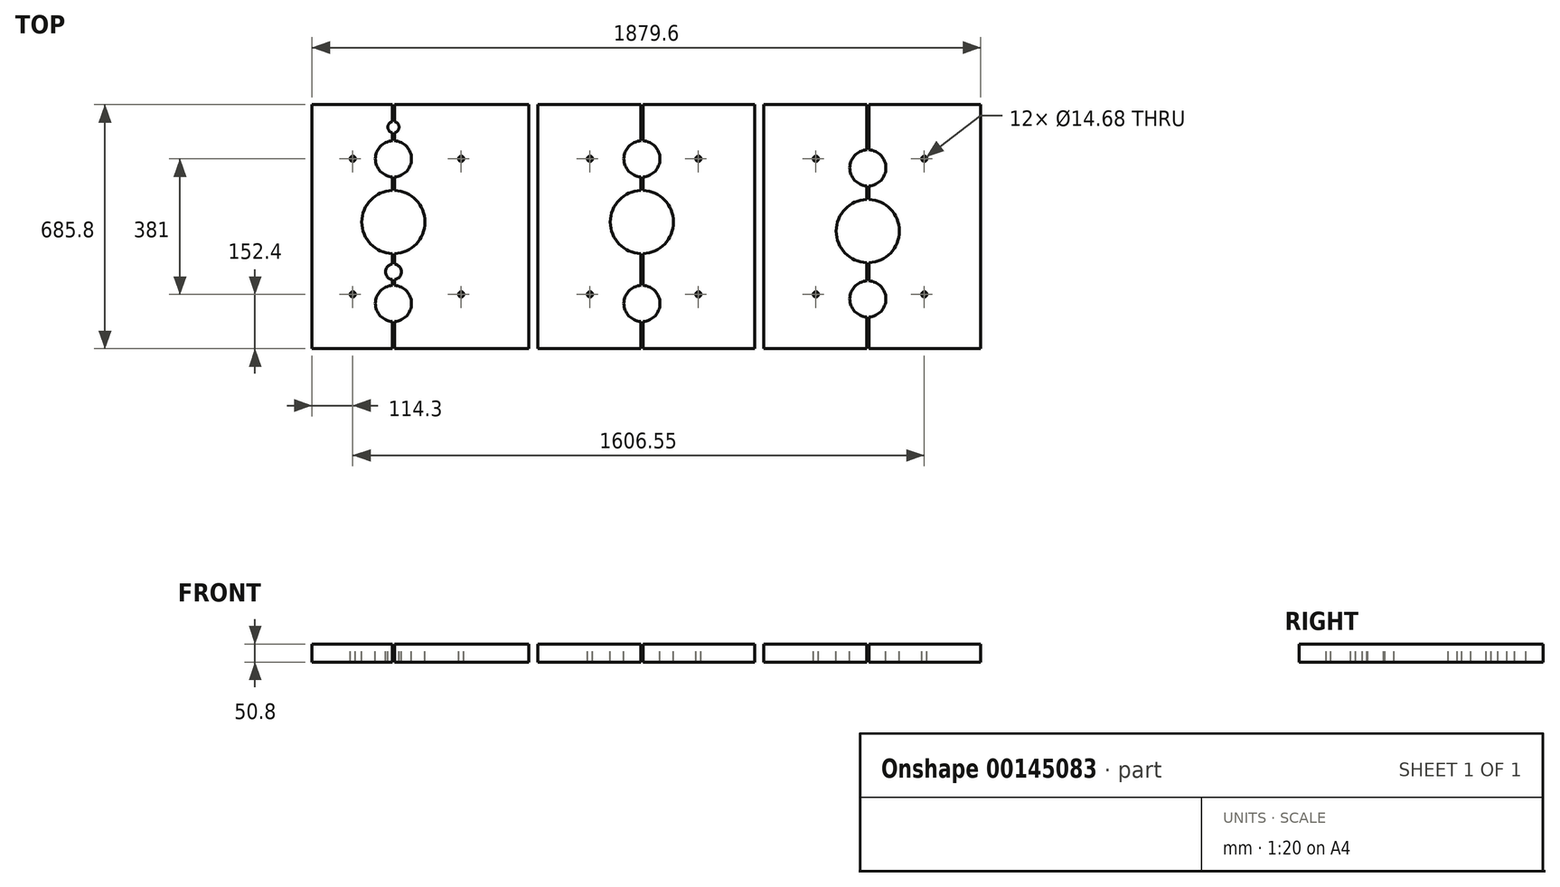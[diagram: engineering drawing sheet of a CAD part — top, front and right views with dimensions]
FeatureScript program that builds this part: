
annotation { "Feature Type Name" : "Feature", "Feature Type Description" : "" }
export const myFeature = defineFeature(function(context is Context, id is Id, definition is map)
    precondition{}
    {
        {
            var Q0;
            Q0=qCreatedBy(makeId("Top.planeOp"),FACE);
            var sketch = newSketch(context, id + "F0", { "sketchPlane" : qUnion([Q0])});
            skLineSegment(sketch, "E0.bottom", {"start": v(0, 685.8) * mm, "end": v(609.6, 685.8) * mm});
            skLineSegment(sketch, "E0.top", {"start": v(0, 0) * mm, "end": v(609.6, 0) * mm});
            skLineSegment(sketch, "E0.left", {"start": v(0, 685.8) * mm, "end": v(0, 0) * mm});
            skLineSegment(sketch, "E0.right", {"start": v(609.6, 685.8) * mm, "end": v(609.6, 0) * mm});
            skSolve(sketch);
        }
        {
            var Q0;
            Q0=makeQuery(id+"F0.imprint","IMPRINT",FACE,{"disambiguationData":[TD([[makeQuery(id+"F0.imprint","IMPRINT",EDGE,{"derivedFrom":sQuery(id+"F0.wireOp",EDGE,"E0.bottom")}),-1.0]])]});
            extrude(context, id + "F1", {"entities" : qUnion([Q0]), "oppositeDirection" : true, "depth" : 50.8 * mm});
        }
        {
            var Q0;
            Q0=makeQuery(id+"F1.opExtrude","CAP_FACE",FACE,{"disambiguationData":[OSD([sQuery(id+"F0.wireOp",EDGE,"E0.bottom"),sQuery(id+"F0.wireOp",EDGE,"E0.top"),sQuery(id+"F0.wireOp",EDGE,"E0.left"),sQuery(id+"F0.wireOp",EDGE,"E0.right")])],"isStart":true});
            var sketch = newSketch(context, id + "F2", { "sketchPlane" : qUnion([Q0])});
            skCircle(sketch, "E1", {"center": v(228.6, 533.4) * mm, "radius": 50.8 * mm});
            skCircle(sketch, "E2", {"center": v(228.6, 355.6) * mm, "radius": 88.9 * mm});
            skCircle(sketch, "E3", {"center": v(228.6, 622.3) * mm, "radius": 15.88 * mm});
            skCircle(sketch, "E4", {"center": v(228.6, 127) * mm, "radius": 50.8 * mm});
            skCircle(sketch, "E5", {"center": v(228.6, 215.9) * mm, "radius": 22.23 * mm});
            skLineSegment(sketch, "E6", {"start": v(114.3, 685.8) * mm, "end": v(114.3, 0) * mm, "construction": true});
            skLineSegment(sketch, "E7", {"start": v(419.1, 685.8) * mm, "end": v(419.1, 0) * mm, "construction": true});
            skPoint(sketch, "E8", {"position": v(419.1, 533.4) * mm});
            skPoint(sketch, "E9", {"position": v(114.3, 533.4) * mm});
            skPoint(sketch, "E10", {"position": v(419.1, 152.4) * mm});
            skPoint(sketch, "E11", {"position": v(114.3, 152.4) * mm});
            skPoint(sketch, "E12", {"position": v(228.6, 0) * mm});
            skLineSegment(sketch, "E13", {"start": v(228.6, 0) * mm, "end": v(0, 0) * mm, "construction": true});
            skLineSegment(sketch, "E14", {"start": v(228.6, 0) * mm, "end": v(609.6, 0) * mm, "construction": true});
            skSolve(sketch);
        }
        {
            var Q0;
            Q0=makeQuery(id+"F2.imprint","IMPRINT",FACE,{"disambiguationData":[TD([[makeQuery(id+"F2.imprint","IMPRINT",EDGE,{"derivedFrom":sQuery(id+"F2.wireOp",EDGE,"E1")}),1.0]])]});
            var Q1;
            Q1=makeQuery(id+"F2.imprint","IMPRINT",FACE,{"disambiguationData":[TD([[makeQuery(id+"F2.imprint","IMPRINT",EDGE,{"derivedFrom":sQuery(id+"F2.wireOp",EDGE,"E4")}),1.0]])]});
            var Q2;
            Q2=makeQuery(id+"F2.imprint","IMPRINT",FACE,{"disambiguationData":[TD([[makeQuery(id+"F2.imprint","IMPRINT",EDGE,{"derivedFrom":sQuery(id+"F2.wireOp",EDGE,"E2")}),1.0]])]});
            var Q3;
            Q3=makeQuery(id+"F2.imprint","IMPRINT",FACE,{"disambiguationData":[TD([[makeQuery(id+"F2.imprint","IMPRINT",EDGE,{"derivedFrom":sQuery(id+"F2.wireOp",EDGE,"E3")}),1.0]])]});
            var Q4;
            Q4=makeQuery(id+"F2.imprint","IMPRINT",FACE,{"disambiguationData":[TD([[makeQuery(id+"F2.imprint","IMPRINT",EDGE,{"derivedFrom":sQuery(id+"F2.wireOp",EDGE,"E5")}),1.0]])]});
            var Q5;
            Q5=makeQuery(id+"F2.imprint","IMPRINT",FACE,{"disambiguationData":[TD([[makeQuery(id+"F2.imprint","IMPRINT",EDGE,{"derivedFrom":sQuery(id+"F2.wireOp",EDGE,"SmzpvA14-N0bI-FcWC-6gtm-8qcKls0d8z8m")}),1.0]])]});
            var Q6;
            Q6=makeQuery(id+"F2.imprint","IMPRINT",FACE,{"disambiguationData":[TD([[makeQuery(id+"F2.imprint","IMPRINT",EDGE,{"derivedFrom":sQuery(id+"F2.wireOp",EDGE,"SVITSdiT-Y995-A8pZ-xzQB-kOccdfRhFBE2")}),1.0]])]});
            var Q7;
            Q7=makeQuery(id+"F2.imprint","IMPRINT",FACE,{"disambiguationData":[TD([[makeQuery(id+"F2.imprint","IMPRINT",EDGE,{"derivedFrom":sQuery(id+"F2.wireOp",EDGE,"RoEeREHV-Iyqc-Nh00-zKd5-UzGnAq062jcI")}),1.0]])]});
            var Q8;
            Q8=makeQuery(id+"F2.imprint","IMPRINT",FACE,{"disambiguationData":[TD([[makeQuery(id+"F2.imprint","IMPRINT",EDGE,{"derivedFrom":sQuery(id+"F2.wireOp",EDGE,"AVpqnPKP-cnh5-tBRG-ZUqZ-7OacRsiV9rUS")}),1.0]])]});
            extrude(context, id + "F3", {"entities" : qUnion([Q0, Q1, Q2, Q3, Q4, Q5, Q6, Q7, Q8]), "operationType" : NewBodyOperationType.REMOVE, "endBound" : BoundingType.THROUGH_ALL, "oppositeDirection" : true, "depth" : 25.4 * mm});
        }
        {
            var Q0;
            Q0=makeQuery(id+"F1.opExtrude","SWEPT_FACE",FACE,{"disambiguationData":[OSD([sQuery(id+"F0.wireOp",EDGE,"E0.right")])]});
            extrude(context, id + "F4", {"entities" : qUnion([Q0]), "depth" : 635 * mm});
        }
        {
            var Q0;
            Q0=makeQuery(id+"F4.opExtrude","SWEPT_BODY",BODY,{"disambiguationData":[OSD([sQuery(id+"F0.wireOp",EDGE,"E0.right")])]});
            deleteBodies(context, id + "F5", {"entities" : qUnion([Q0])});
        }
        {
            var Q0;
            Q0=makeQuery(id+"F1.opExtrude","SWEPT_BODY",BODY,{"disambiguationData":[OSD([sQuery(id+"F0.wireOp",EDGE,"E0.bottom"),sQuery(id+"F0.wireOp",EDGE,"E0.top"),sQuery(id+"F0.wireOp",EDGE,"E0.left"),sQuery(id+"F0.wireOp",EDGE,"E0.right")])]});
            transform(context, id + "F6", {"entities" : qUnion([Q0]), "transformType" : TransformType.COPY});
        }
        {
            var Q0;
            Q0=makeQuery(id+"F1.opExtrude","SWEPT_BODY",BODY,{"disambiguationData":[OSD([sQuery(id+"F0.wireOp",EDGE,"E0.bottom"),sQuery(id+"F0.wireOp",EDGE,"E0.top"),sQuery(id+"F0.wireOp",EDGE,"E0.left"),sQuery(id+"F0.wireOp",EDGE,"E0.right")])]});
            transform(context, id + "F7", {"entities" : qUnion([Q0]), "transformType" : TransformType.COPY});
        }
        {
            var Q0;
            Q0=makeQuery(id+"F6.opPattern","COPY",BODY,{"derivedFrom":makeQuery(id+"F1.opExtrude","SWEPT_BODY",BODY,{"disambiguationData":[OSD([sQuery(id+"F0.wireOp",EDGE,"E0.bottom"),sQuery(id+"F0.wireOp",EDGE,"E0.top"),sQuery(id+"F0.wireOp",EDGE,"E0.left"),sQuery(id+"F0.wireOp",EDGE,"E0.right")])]}),"instanceName":"1"});
            var Q1;
            Q1=makeQuery(id+"F6.opPattern","COPY",FACE,{"derivedFrom":makeQuery(id+"F1.opExtrude","SWEPT_FACE",FACE,{"disambiguationData":[OSD([sQuery(id+"F0.wireOp",EDGE,"E0.right")])]}),"instanceName":"1"});
            transform(context, id + "F8", {"entities" : qUnion([Q0]), "transformType" : TransformType.TRANSLATION_DISTANCE, "transformDirection" : qUnion([Q1]), "distance" : 635 * mm, "makeCopy" : false});
        }
        {
            var Q0;
            Q0=makeQuery(id+"F7.opPattern","COPY",BODY,{"derivedFrom":makeQuery(id+"F1.opExtrude","SWEPT_BODY",BODY,{"disambiguationData":[OSD([sQuery(id+"F0.wireOp",EDGE,"E0.bottom"),sQuery(id+"F0.wireOp",EDGE,"E0.top"),sQuery(id+"F0.wireOp",EDGE,"E0.left"),sQuery(id+"F0.wireOp",EDGE,"E0.right")])]}),"instanceName":"1"});
            var Q1;
            Q1=makeQuery(id+"F7.opPattern","COPY",FACE,{"derivedFrom":makeQuery(id+"F1.opExtrude","SWEPT_FACE",FACE,{"disambiguationData":[OSD([sQuery(id+"F0.wireOp",EDGE,"E0.right")])]}),"instanceName":"1"});
            transform(context, id + "F9", {"entities" : qUnion([Q0]), "transformType" : TransformType.TRANSLATION_DISTANCE, "transformDirection" : qUnion([Q1]), "distance" : 1270 * mm, "makeCopy" : false});
        }
        {
            var Q0;
            Q0=makeQuery(id+"F6.opPattern","COPY",FACE,{"derivedFrom":makeQuery(id+"F1.opExtrude","SWEPT_FACE",FACE,{"disambiguationData":[OSD([sQuery(id+"F0.wireOp",EDGE,"E0.bottom")])]}),"instanceName":"1"});
            var Q1;
            Q1=makeQuery(id+"F6.opPattern","COPY",FACE,{"derivedFrom":makeQuery(id+"F1.opExtrude","SWEPT_FACE",FACE,{"disambiguationData":[OSD([sQuery(id+"F0.wireOp",EDGE,"E0.top")])]}),"instanceName":"1"});
            extrude(context, id + "F10", {"entities" : qUnion([Q0]), "operationType" : NewBodyOperationType.ADD, "endBound" : BoundingType.UP_TO_SURFACE, "oppositeDirection" : true, "endBoundEntityFace" : qUnion([Q1]), "depth" : 25.4 * mm});
        }
        {
            var Q0;
            {var subQ0=sQuery(id+"F0.wireOp",EDGE,"E0.bottom");Q0=makeQuery(id+"F10.boolean.opBoolean","MERGE",FACE,{"derivedFrom":[makeQuery(id+"F6.opPattern","COPY",FACE,{"derivedFrom":makeQuery(id+"F1.opExtrude","CAP_FACE",FACE,{"disambiguationData":[OSD([subQ0,sQuery(id+"F0.wireOp",EDGE,"E0.top"),sQuery(id+"F0.wireOp",EDGE,"E0.left"),sQuery(id+"F0.wireOp",EDGE,"E0.right")])],"isStart":true}),"instanceName":"1"}),makeQuery(id+"F10.opExtrude","SWEPT_FACE",FACE,{"disambiguationData":[OSD([subQ0]),TDD([makeQuery(id+"F6.opPattern","COPY",EDGE,{"derivedFrom":makeQuery(id+"F1.opExtrude","CAP_EDGE",EDGE,{"disambiguationData":[OSD([subQ0])],"isStart":true}),"instanceName":"1"})])]})]});}
            var sketch = newSketch(context, id + "F11", { "sketchPlane" : qUnion([Q0])});
            skCircle(sketch, "E15", {"center": v(927.1, 533.4) * mm, "radius": 50.8 * mm});
            skCircle(sketch, "E16", {"center": v(927.1, 355.6) * mm, "radius": 88.9 * mm});
            skCircle(sketch, "E17", {"center": v(927.1, 127) * mm, "radius": 50.8 * mm});
            skLineSegment(sketch, "E18", {"start": v(781.05, 685.8) * mm, "end": v(781.05, 0) * mm, "construction": true});
            skLineSegment(sketch, "E19", {"start": v(1085.85, 685.8) * mm, "end": v(1085.85, 0) * mm, "construction": true});
            skPoint(sketch, "E20", {"position": v(781.05, 533.4) * mm});
            skPoint(sketch, "E21", {"position": v(1085.85, 533.4) * mm});
            skPoint(sketch, "E22", {"position": v(781.05, 152.4) * mm});
            skPoint(sketch, "E23", {"position": v(1085.85, 152.4) * mm});
            skPoint(sketch, "E24", {"position": v(927.1, 0) * mm});
            skLineSegment(sketch, "E25", {"start": v(927.1, 0) * mm, "end": v(635, 0) * mm, "construction": true});
            skLineSegment(sketch, "E26", {"start": v(927.1, 0) * mm, "end": v(1244.6, 0) * mm, "construction": true});
            skSolve(sketch);
        }
        {
            var Q0;
            Q0 = qSketchRegion(id + "F11", true);
            var Q1;
            {var subQ0=sQuery(id+"F0.wireOp",EDGE,"E0.bottom");Q1=makeQuery(id+"F10.boolean.opBoolean","MERGE",FACE,{"derivedFrom":[makeQuery(id+"F6.opPattern","COPY",FACE,{"derivedFrom":makeQuery(id+"F1.opExtrude","CAP_FACE",FACE,{"disambiguationData":[OSD([subQ0,sQuery(id+"F0.wireOp",EDGE,"E0.top"),sQuery(id+"F0.wireOp",EDGE,"E0.left"),sQuery(id+"F0.wireOp",EDGE,"E0.right")])],"isStart":false}),"instanceName":"1"}),makeQuery(id+"F10.opExtrude","SWEPT_FACE",FACE,{"disambiguationData":[OSD([subQ0]),TDD([makeQuery(id+"F6.opPattern","COPY",EDGE,{"derivedFrom":makeQuery(id+"F1.opExtrude","CAP_EDGE",EDGE,{"disambiguationData":[OSD([subQ0])],"isStart":false}),"instanceName":"1"})])]})]});}
            extrude(context, id + "F12", {"entities" : qUnion([Q0]), "operationType" : NewBodyOperationType.REMOVE, "endBound" : BoundingType.UP_TO_SURFACE, "oppositeDirection" : true, "endBoundEntityFace" : qUnion([Q1]), "depth" : 25.4 * mm});
        }
        {
            var Q0;
            Q0=makeQuery(id+"F7.opPattern","COPY",FACE,{"derivedFrom":makeQuery(id+"F1.opExtrude","SWEPT_FACE",FACE,{"disambiguationData":[OSD([sQuery(id+"F0.wireOp",EDGE,"E0.bottom")])]}),"instanceName":"1"});
            var Q1;
            Q1=makeQuery(id+"F7.opPattern","COPY",FACE,{"derivedFrom":makeQuery(id+"F1.opExtrude","SWEPT_FACE",FACE,{"disambiguationData":[OSD([sQuery(id+"F0.wireOp",EDGE,"E0.top")])]}),"instanceName":"1"});
            extrude(context, id + "F13", {"entities" : qUnion([Q0]), "operationType" : NewBodyOperationType.ADD, "endBound" : BoundingType.UP_TO_SURFACE, "oppositeDirection" : true, "endBoundEntityFace" : qUnion([Q1]), "depth" : 25.4 * mm});
        }
        {
            var Q0;
            {var subQ0=sQuery(id+"F0.wireOp",EDGE,"E0.bottom");Q0=makeQuery(id+"F13.boolean.opBoolean","MERGE",FACE,{"derivedFrom":[makeQuery(id+"F7.opPattern","COPY",FACE,{"derivedFrom":makeQuery(id+"F1.opExtrude","CAP_FACE",FACE,{"disambiguationData":[OSD([subQ0,sQuery(id+"F0.wireOp",EDGE,"E0.top"),sQuery(id+"F0.wireOp",EDGE,"E0.left"),sQuery(id+"F0.wireOp",EDGE,"E0.right")])],"isStart":true}),"instanceName":"1"}),makeQuery(id+"F13.opExtrude","SWEPT_FACE",FACE,{"disambiguationData":[OSD([subQ0]),TDD([makeQuery(id+"F7.opPattern","COPY",EDGE,{"derivedFrom":makeQuery(id+"F1.opExtrude","CAP_EDGE",EDGE,{"disambiguationData":[OSD([subQ0])],"isStart":true}),"instanceName":"1"})])]})]});}
            var sketch = newSketch(context, id + "F14", { "sketchPlane" : qUnion([Q0])});
            skCircle(sketch, "E27", {"center": v(1562.1, 508) * mm, "radius": 50.8 * mm});
            skCircle(sketch, "E28", {"center": v(1562.1, 330.2) * mm, "radius": 88.9 * mm});
            skCircle(sketch, "E29", {"center": v(1562.1, 139.7) * mm, "radius": 50.8 * mm});
            skLineSegment(sketch, "E30", {"start": v(1416.05, 685.8) * mm, "end": v(1416.05, 0) * mm, "construction": true});
            skLineSegment(sketch, "E31", {"start": v(1720.85, 685.8) * mm, "end": v(1720.85, 0) * mm, "construction": true});
            skPoint(sketch, "E32", {"position": v(1416.05, 533.4) * mm});
            skPoint(sketch, "E33", {"position": v(1720.85, 533.4) * mm});
            skPoint(sketch, "E34", {"position": v(1416.05, 152.4) * mm});
            skPoint(sketch, "E35", {"position": v(1720.85, 152.4) * mm});
            skPoint(sketch, "E36", {"position": v(1562.1, 0) * mm});
            skLineSegment(sketch, "E37", {"start": v(1562.1, 0) * mm, "end": v(1270, 0) * mm, "construction": true});
            skLineSegment(sketch, "E38", {"start": v(1562.1, 0) * mm, "end": v(1879.6, 0) * mm, "construction": true});
            skSolve(sketch);
        }
        {
            var Q0;
            Q0 = qSketchRegion(id + "F14", true);
            extrude(context, id + "F15", {"entities" : qUnion([Q0]), "operationType" : NewBodyOperationType.REMOVE, "endBound" : BoundingType.UP_TO_NEXT, "oppositeDirection" : true, "depth" : 25.4 * mm});
        }
        {
            var Q0;
            Q0=makeQuery(id+"F1.opExtrude","SWEPT_FACE",FACE,{"disambiguationData":[OSD([sQuery(id+"F0.wireOp",EDGE,"E0.top")])]});
            var sketch = newSketch(context, id + "F16", { "sketchPlane" : qUnion([Q0])});
            skLineSegment(sketch, "E39.bottom", {"start": v(923.93, -50.8) * mm, "end": v(930.28, -50.8) * mm});
            skLineSegment(sketch, "E39.top", {"start": v(923.93, 0) * mm, "end": v(930.28, 0) * mm});
            skLineSegment(sketch, "E39.left", {"start": v(923.93, -50.8) * mm, "end": v(923.93, 0) * mm});
            skLineSegment(sketch, "E39.right", {"start": v(930.28, -50.8) * mm, "end": v(930.28, 0) * mm});
            skLineSegment(sketch, "E40.bottom", {"start": v(1558.92, -50.8) * mm, "end": v(1565.27, -50.8) * mm});
            skLineSegment(sketch, "E40.top", {"start": v(1558.92, 0) * mm, "end": v(1565.27, 0) * mm});
            skLineSegment(sketch, "E40.left", {"start": v(1558.92, -50.8) * mm, "end": v(1558.92, 0) * mm});
            skLineSegment(sketch, "E40.right", {"start": v(1565.27, -50.8) * mm, "end": v(1565.27, 0) * mm});
            skLineSegment(sketch, "E41.bottom", {"start": v(225.43, 0) * mm, "end": v(231.78, 0) * mm});
            skLineSegment(sketch, "E41.top", {"start": v(225.43, -50.8) * mm, "end": v(231.78, -50.8) * mm});
            skLineSegment(sketch, "E41.left", {"start": v(225.43, 0) * mm, "end": v(225.43, -50.8) * mm});
            skLineSegment(sketch, "E41.right", {"start": v(231.78, 0) * mm, "end": v(231.78, -50.8) * mm});
            skSolve(sketch);
        }
        {
            var Q0;
            Q0=makeQuery(id+"F16.imprint","IMPRINT",FACE,{"disambiguationData":[TD([[makeQuery(id+"F16.imprint","IMPRINT",EDGE,{"derivedFrom":sQuery(id+"F16.wireOp",EDGE,"E41.bottom")}),-1.0]])]});
            var Q1;
            Q1=makeQuery(id+"F16.imprint","IMPRINT",FACE,{"disambiguationData":[TD([[makeQuery(id+"F16.imprint","IMPRINT",EDGE,{"derivedFrom":sQuery(id+"F16.wireOp",EDGE,"E39.bottom")}),1.0]])]});
            var Q2;
            Q2=makeQuery(id+"F16.imprint","IMPRINT",FACE,{"disambiguationData":[TD([[makeQuery(id+"F16.imprint","IMPRINT",EDGE,{"derivedFrom":sQuery(id+"F16.wireOp",EDGE,"E40.bottom")}),1.0]])]});
            extrude(context, id + "F17", {"entities" : qUnion([Q0, Q1, Q2]), "operationType" : NewBodyOperationType.REMOVE, "endBound" : BoundingType.THROUGH_ALL, "oppositeDirection" : true, "depth" : 25.4 * mm});
        }
        {
            var Q0;
            Q0=sQuery(id+"F2.wireOp",VERTEX,"E9");
            var Q1;
            Q1=sQuery(id+"F2.wireOp",VERTEX,"E11");
            var Q2;
            Q2=sQuery(id+"F2.wireOp",VERTEX,"E8");
            var Q3;
            Q3=sQuery(id+"F2.wireOp",VERTEX,"E10");
            var Q4;
            Q4=makeQuery(id+"F17.boolean.opBoolean","SPLIT",BODY,{"disambiguationData":[OD(0.0)],"derivedFrom":makeQuery(id+"F1.opExtrude","SWEPT_BODY",BODY,{"disambiguationData":[OSD([sQuery(id+"F0.wireOp",EDGE,"E0.bottom"),sQuery(id+"F0.wireOp",EDGE,"E0.top"),sQuery(id+"F0.wireOp",EDGE,"E0.left"),sQuery(id+"F0.wireOp",EDGE,"E0.right")])]})});
            var Q5;
            Q5=makeQuery(id+"F17.boolean.opBoolean","SPLIT",BODY,{"disambiguationData":[OD(1.0)],"derivedFrom":makeQuery(id+"F1.opExtrude","SWEPT_BODY",BODY,{"disambiguationData":[OSD([sQuery(id+"F0.wireOp",EDGE,"E0.bottom"),sQuery(id+"F0.wireOp",EDGE,"E0.top"),sQuery(id+"F0.wireOp",EDGE,"E0.left"),sQuery(id+"F0.wireOp",EDGE,"E0.right")])]})});
            hole(context, id + "F18", {"style" : HoleStyle.SIMPLE, "endStyle" : HoleEndStyle.THROUGH, "standardTappedOrClearance" : lookupTablePath({ "standard" : "ANSI", "engagement" : "75%", "pitch" : "18 tpi", "size" : "5/8", "type" : "Tapped" }), "standardBlindInLast" : lookupTablePath({ "standard" : "ANSI", "engagement" : "75%", "pitch" : "18 tpi", "size" : "5/8", "type" : "Tapped" }), "holeDiameter" : 14.68 * mm, "locations" : qUnion([Q0, Q1, Q2, Q3]), "scope" : qUnion([Q4, Q5]), "isTappedThrough" : true, "majorDiameter" : 15.88 * mm, "showTappedDepth" : true});
        }
        {
            var Q0;
            Q0=sQuery(id+"F11.wireOp",VERTEX,"E20");
            var Q1;
            Q1=sQuery(id+"F11.wireOp",VERTEX,"E21");
            var Q2;
            Q2=sQuery(id+"F11.wireOp",VERTEX,"E23");
            var Q3;
            Q3=sQuery(id+"F11.wireOp",VERTEX,"E22");
            var Q4;
            Q4=makeQuery(id+"F17.boolean.opBoolean","SPLIT",BODY,{"disambiguationData":[OD(0.0)],"derivedFrom":makeQuery(id+"F6.opPattern","COPY",BODY,{"derivedFrom":makeQuery(id+"F1.opExtrude","SWEPT_BODY",BODY,{"disambiguationData":[OSD([sQuery(id+"F0.wireOp",EDGE,"E0.bottom"),sQuery(id+"F0.wireOp",EDGE,"E0.top"),sQuery(id+"F0.wireOp",EDGE,"E0.left"),sQuery(id+"F0.wireOp",EDGE,"E0.right")])]}),"instanceName":"1"})});
            var Q5;
            Q5=makeQuery(id+"F17.boolean.opBoolean","SPLIT",BODY,{"disambiguationData":[OD(1.0)],"derivedFrom":makeQuery(id+"F6.opPattern","COPY",BODY,{"derivedFrom":makeQuery(id+"F1.opExtrude","SWEPT_BODY",BODY,{"disambiguationData":[OSD([sQuery(id+"F0.wireOp",EDGE,"E0.bottom"),sQuery(id+"F0.wireOp",EDGE,"E0.top"),sQuery(id+"F0.wireOp",EDGE,"E0.left"),sQuery(id+"F0.wireOp",EDGE,"E0.right")])]}),"instanceName":"1"})});
            hole(context, id + "F19", {"style" : HoleStyle.SIMPLE, "endStyle" : HoleEndStyle.THROUGH, "standardTappedOrClearance" : lookupTablePath({ "standard" : "ANSI", "engagement" : "75%", "pitch" : "18 tpi", "size" : "5/8", "type" : "Tapped" }), "standardBlindInLast" : lookupTablePath({ "standard" : "ANSI", "engagement" : "75%", "pitch" : "18 tpi", "size" : "5/8", "type" : "Tapped" }), "holeDiameter" : 14.68 * mm, "locations" : qUnion([Q0, Q1, Q2, Q3]), "scope" : qUnion([Q4, Q5]), "isTappedThrough" : true, "majorDiameter" : 15.88 * mm, "showTappedDepth" : true});
        }
        {
            var Q0;
            Q0=sQuery(id+"F14.wireOp",VERTEX,"E32");
            var Q1;
            Q1=sQuery(id+"F14.wireOp",VERTEX,"E33");
            var Q2;
            Q2=sQuery(id+"F14.wireOp",VERTEX,"E34");
            var Q3;
            Q3=sQuery(id+"F14.wireOp",VERTEX,"E35");
            var Q4;
            Q4=makeQuery(id+"F17.boolean.opBoolean","SPLIT",BODY,{"disambiguationData":[OD(0.0)],"derivedFrom":makeQuery(id+"F7.opPattern","COPY",BODY,{"derivedFrom":makeQuery(id+"F1.opExtrude","SWEPT_BODY",BODY,{"disambiguationData":[OSD([sQuery(id+"F0.wireOp",EDGE,"E0.bottom"),sQuery(id+"F0.wireOp",EDGE,"E0.top"),sQuery(id+"F0.wireOp",EDGE,"E0.left"),sQuery(id+"F0.wireOp",EDGE,"E0.right")])]}),"instanceName":"1"})});
            var Q5;
            Q5=makeQuery(id+"F17.boolean.opBoolean","SPLIT",BODY,{"disambiguationData":[OD(1.0)],"derivedFrom":makeQuery(id+"F7.opPattern","COPY",BODY,{"derivedFrom":makeQuery(id+"F1.opExtrude","SWEPT_BODY",BODY,{"disambiguationData":[OSD([sQuery(id+"F0.wireOp",EDGE,"E0.bottom"),sQuery(id+"F0.wireOp",EDGE,"E0.top"),sQuery(id+"F0.wireOp",EDGE,"E0.left"),sQuery(id+"F0.wireOp",EDGE,"E0.right")])]}),"instanceName":"1"})});
            hole(context, id + "F20", {"style" : HoleStyle.SIMPLE, "endStyle" : HoleEndStyle.THROUGH, "standardTappedOrClearance" : lookupTablePath({ "standard" : "ANSI", "engagement" : "75%", "pitch" : "18 tpi", "size" : "5/8", "type" : "Tapped" }), "standardBlindInLast" : lookupTablePath({ "standard" : "ANSI", "engagement" : "75%", "pitch" : "18 tpi", "size" : "5/8", "type" : "Tapped" }), "holeDiameter" : 14.68 * mm, "locations" : qUnion([Q0, Q1, Q2, Q3]), "scope" : qUnion([Q4, Q5]), "isTappedThrough" : true, "majorDiameter" : 15.88 * mm, "showTappedDepth" : true});
        }
    });
